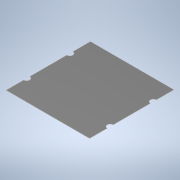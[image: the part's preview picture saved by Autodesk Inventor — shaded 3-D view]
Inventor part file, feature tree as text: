
AUTODESK INVENTOR PART (.ipt)
format: ipt  version: 2022 (Build 260153000, 153)  size: 120,320 bytes
history: native  units: in
note: dims shown in document units (in); Inventor stores cm internally (conversion verified against a paired STEP export)
features: extrude x2, sketch x2
ambient origin geometry x8: Origin, YZ Plane, XZ Plane, XY Plane, X Axis, Y Axis, Z Axis, Center Point
bodies: Solid1 (feature_tree)
feature tree (4):
  extrude  "Extrusion1"  Depth=1.6378in
  extrude  "Extrusion2"  Depth=0.0591in
  sketch  "Sketch1"  dims[d0=1.6535in d1=1.6378in]
  sketch  "Sketch2"  dims[d2=0.0031in d3=0.0in d5=0.0591in d6=0.0in d7=0.0in d8=0.1181in d9=0.4045in]
